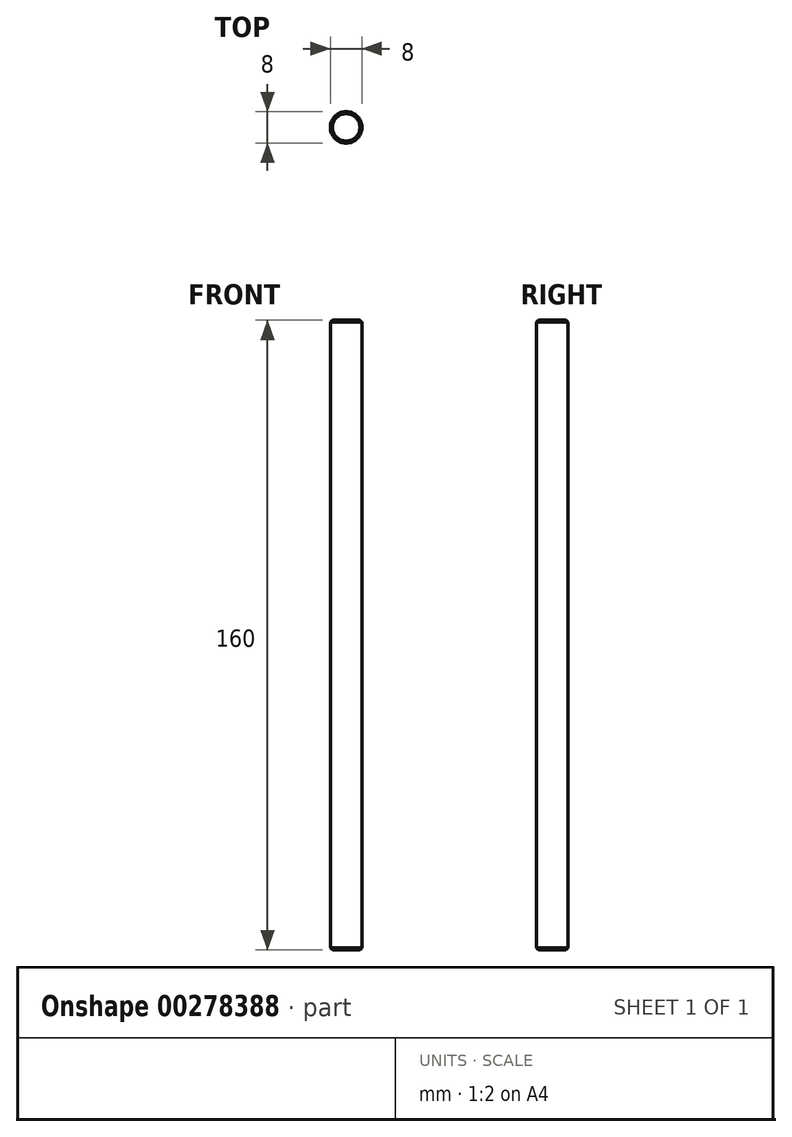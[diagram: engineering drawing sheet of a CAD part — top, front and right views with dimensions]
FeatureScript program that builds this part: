
annotation { "Feature Type Name" : "Feature", "Feature Type Description" : "" }
export const myFeature = defineFeature(function(context is Context, id is Id, definition is map)
    precondition{}
    {
        {
            var Q0;
            Q0=qCreatedBy(makeId("Top.planeOp"),FACE);
            var sketch = newSketch(context, id + "F0", { "sketchPlane" : qUnion([Q0])});
            skCircle(sketch, "E0", {"center": v(0, 0) * mm, "radius": 4 * mm});
            skSolve(sketch);
        }
        {
            var Q0;
            Q0 = qSketchRegion(id + "F0", true);
            extrude(context, id + "F1", {"entities" : qUnion([Q0]), "offsetDistance" : 25 * mm, "depth" : 160 * mm});
        }
        {
            var Q0;
            Q0=makeQuery(id+"F1.opExtrude","SWEPT_FACE",FACE,{"disambiguationData":[OSD([sQuery(id+"F0.wireOp",EDGE,"E0")])]});
            chamfer(context, id + "F2", {"entities" : qUnion([Q0]), "width" : 0.5 * mm, "tangentPropagation" : true});
        }
    });
